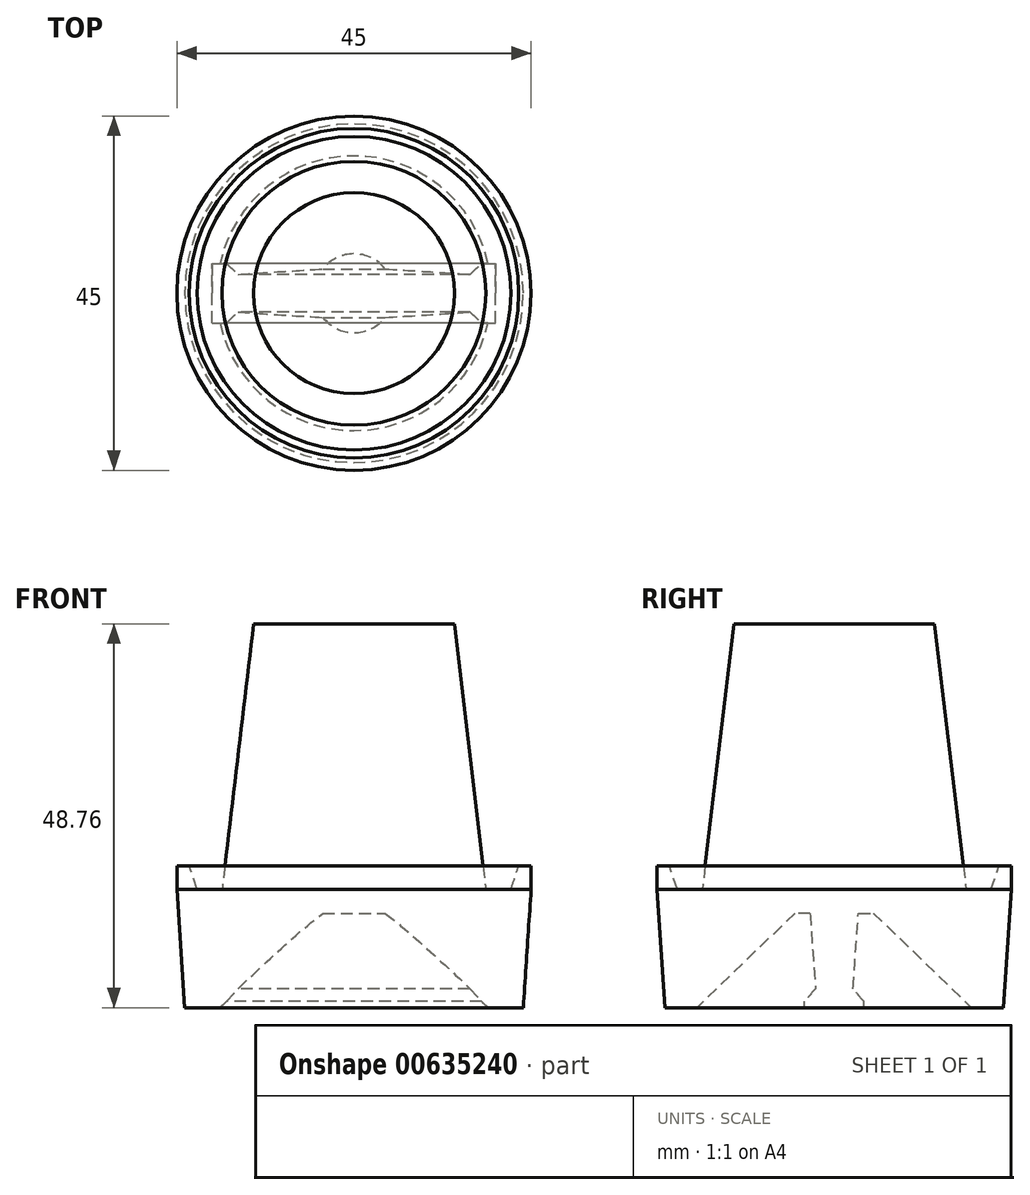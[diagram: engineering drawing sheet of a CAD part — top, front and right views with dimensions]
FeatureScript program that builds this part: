
annotation { "Feature Type Name" : "Feature", "Feature Type Description" : "" }
export const myFeature = defineFeature(function(context is Context, id is Id, definition is map)
    precondition{}
    {
        {
            var Q0;
            Q0=qCreatedBy(makeId("Top.planeOp"),FACE);
            var sketch = newSketch(context, id + "F0", { "sketchPlane" : qUnion([Q0])});
            skCircle(sketch, "E0", {"center": v(0, 0) * mm, "radius": 22.5 * mm});
            skSolve(sketch);
        }
        {
            var Q0;
            Q0=makeQuery(id+"F0.imprint","IMPRINT",FACE,{"disambiguationData":[TD([[makeQuery(id+"F0.imprint","IMPRINT",EDGE,{"derivedFrom":sQuery(id+"F0.wireOp",EDGE,"E0")}),1.0]])]});
            extrude(context, id + "F1", {"entities" : qUnion([Q0]), "depth" : -15 * mm, "offsetDistance" : 25 * mm});
        }
        {
            var Q0;
            Q0=qCreatedBy(makeId("Right.planeOp"),FACE);
            var sketch = newSketch(context, id + "F2", { "sketchPlane" : qUnion([Q0])});
            skLineSegment(sketch, "E1", {"start": v(17.65, -15.2) * mm, "end": v(5, -3.03) * mm});
            skLineSegment(sketch, "E2", {"start": v(5, -3.03) * mm, "end": v(0, -3.03) * mm});
            skLineSegment(sketch, "E3", {"start": v(0, -3.03) * mm, "end": v(0, -15.2) * mm});
            skLineSegment(sketch, "E4", {"start": v(0, -15.2) * mm, "end": v(17.65, -15.2) * mm});
            skSolve(sketch);
        }
        {
            var Q0;
            Q0 = qSketchRegion(id + "F2", true);
            var Q1;
            Q1=sQuery(id+"F2.wireOp",EDGE,"E3");
            revolve(context, id + "F3", {"operationType" : NewBodyOperationType.REMOVE, "entities" : qUnion([Q0]), "axis" : qUnion([Q1]), "revolveType" : RevolveType.FULL, "oppositeDirection" : true});
        }
        {
            var Q0;
            Q0=qCreatedBy(makeId("Right.planeOp"),FACE);
            var sketch = newSketch(context, id + "F4", { "sketchPlane" : qUnion([Q0])});
            skLineSegment(sketch, "E5", {"start": v(3.77, -15) * mm, "end": v(3.77, -14.23) * mm});
            skLineSegment(sketch, "E6", {"start": v(3.77, -14.23) * mm, "end": v(2.38, -12.58) * mm});
            skLineSegment(sketch, "E7", {"start": v(2.38, -12.58) * mm, "end": v(3.08, -2.86) * mm});
            skLineSegment(sketch, "E8", {"start": v(3.08, -2.86) * mm, "end": v(0, -2.86) * mm});
            skLineSegment(sketch, "E9", {"start": v(3.77, -15) * mm, "end": v(0, -15) * mm});
            skLineSegment(sketch, "E10.MirrorCS", {"start": v(-3.77, -15) * mm, "end": v(0, -15) * mm});
            skLineSegment(sketch, "E11.MirrorCS", {"start": v(-3.77, -15) * mm, "end": v(-3.77, -14.23) * mm});
            skLineSegment(sketch, "E12.MirrorCS", {"start": v(-3.77, -14.23) * mm, "end": v(-2.38, -12.58) * mm});
            skLineSegment(sketch, "E13.MirrorCS", {"start": v(-2.38, -12.58) * mm, "end": v(-3.08, -2.86) * mm});
            skLineSegment(sketch, "E14.MirrorCS", {"start": v(-3.08, -2.86) * mm, "end": v(0, -2.86) * mm});
            skSolve(sketch);
        }
        {
            var Q0;
            Q0 = qSketchRegion(id + "F4", true);
            extrude(context, id + "F5", {"entities" : qUnion([Q0]), "operationType" : NewBodyOperationType.ADD, "endBound" : BoundingType.SYMMETRIC, "depth" : 36 * mm, "offsetDistance" : 25 * mm});
        }
        {
            var Q0;
            Q0=qCreatedBy(makeId("Front.planeOp"),FACE);
            var sketch = newSketch(context, id + "F6", { "sketchPlane" : qUnion([Q0])});
            skLineSegment(sketch, "E15", {"start": v(0, 0) * mm, "end": v(0, 160.4) * mm});
            skLineSegment(sketch, "E16", {"start": v(0, 0) * mm, "end": v(16.75, 0) * mm});
            skLineSegment(sketch, "E17", {"start": v(16.75, 0) * mm, "end": v(12.76, 33.76) * mm});
            skLineSegment(sketch, "E18", {"start": v(12.75, -2.4) * mm, "end": v(16.75, 0) * mm});
            skLineSegment(sketch, "E19", {"start": v(12.76, 33.76) * mm, "end": v(0, 33.76) * mm});
            skLineSegment(sketch, "E20", {"start": v(0, 33.76) * mm, "end": v(0, 0) * mm});
            skLineSegment(sketch, "E21", {"start": v(12.75, -2.4) * mm, "end": v(0, 0) * mm});
            skSolve(sketch);
        }
        {
            var Q0;
            {var subQ0=sQuery(id+"F6.wireOp",EDGE,"NOqFsPqD-XFDb-L3v0-IgoA-eCUBzX9nZBsb");Q0=makeQuery(id+"F6.imprint","IMPRINT",FACE,{"disambiguationData":[TD([[makeQuery(id+"F6.imprint","IMPRINT",EDGE,{"derivedFrom":subQ0}),1.0]])]});}
            var Q1;
            Q1=makeQuery(id+"F6.imprint","IMPRINT",FACE,{"disambiguationData":[TD([[makeQuery(id+"F6.imprint","IMPRINT",EDGE,{"derivedFrom":sQuery(id+"F6.wireOp",EDGE,"E16")}),1.0]])]});
            var Q2;
            Q2=sQuery(id+"F6.wireOp",EDGE,"E15");
            revolve(context, id + "F7", {"operationType" : NewBodyOperationType.ADD, "entities" : qUnion([Q0, Q1]), "axis" : qUnion([Q2]), "revolveType" : RevolveType.FULL});
        }
        {
            var Q0;
            Q0=makeQuery(id+"F1.opExtrude","CAP_EDGE",EDGE,{"disambiguationData":[OSD([sQuery(id+"F0.wireOp",EDGE,"E0")])],"isStart":false});
            chamfer(context, id + "F8", {"entities" : qUnion([Q0]), "chamferType" : ChamferType.TWO_OFFSETS, "width1" : 15 * mm, "oppositeDirection" : false, "width2" : 1 * mm, "tangentPropagation" : true});
        }
        {
            var Q0;
            Q0=qCreatedBy(makeId("Top.planeOp"),FACE);
            var sketch = newSketch(context, id + "F9", { "sketchPlane" : qUnion([Q0])});
            skCircle(sketch, "E22", {"center": v(0, 0) * mm, "radius": 22.5 * mm});
            skCircle(sketch, "E23", {"center": v(0, 0) * mm, "radius": 19.92 * mm});
            skSolve(sketch);
        }
        {
            var Q0;
            Q0=makeQuery(id+"F9.imprint","IMPRINT",FACE,{"disambiguationData":[TD([[makeQuery(id+"F9.imprint","IMPRINT",EDGE,{"derivedFrom":sQuery(id+"F9.wireOp",EDGE,"E22")}),1.0]])]});
            extrude(context, id + "F10", {"entities" : qUnion([Q0]), "operationType" : NewBodyOperationType.ADD, "depth" : 3 * mm, "offsetDistance" : 25 * mm});
        }
        {
            var Q0;
            Q0=makeQuery(id+"F10.opExtrude","CAP_EDGE",EDGE,{"disambiguationData":[OSD([sQuery(id+"F9.wireOp",EDGE,"E23")])],"isStart":false});
            chamfer(context, id + "F11", {"entities" : qUnion([Q0]), "chamferType" : ChamferType.TWO_OFFSETS, "width1" : 3 * mm, "oppositeDirection" : false, "width2" : 1 * mm, "tangentPropagation" : true});
        }
    });
